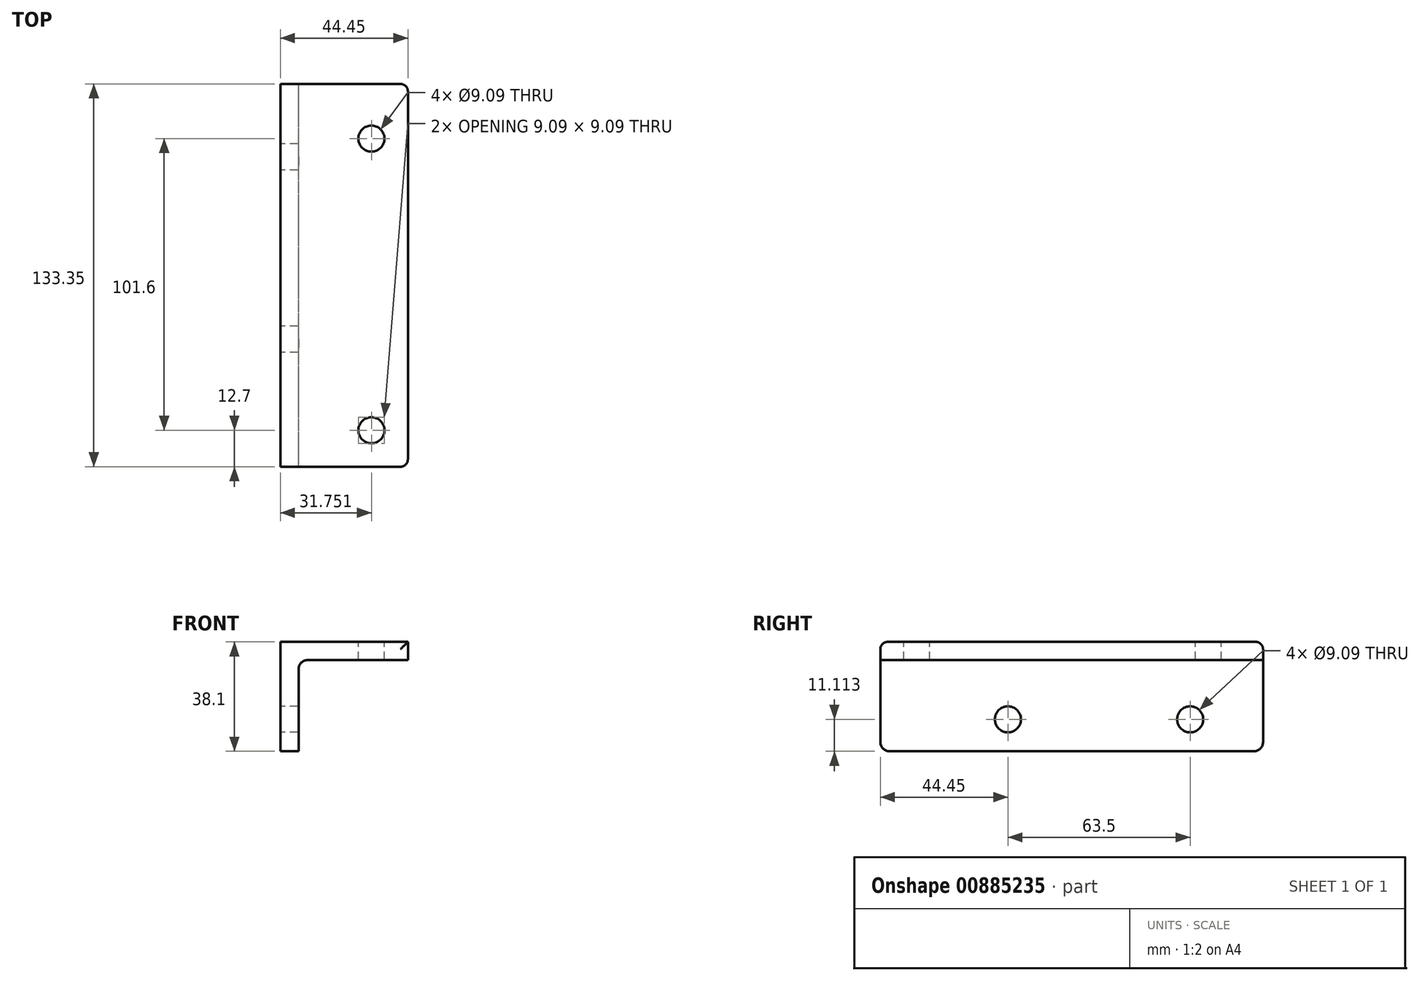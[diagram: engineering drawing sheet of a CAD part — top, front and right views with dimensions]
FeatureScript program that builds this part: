
annotation { "Feature Type Name" : "Feature", "Feature Type Description" : "" }
export const myFeature = defineFeature(function(context is Context, id is Id, definition is map)
    precondition{}
    {
        {
            var Q0;
            Q0=qCreatedBy(makeId("Front.planeOp"),FACE);
            var sketch = newSketch(context, id + "F0", { "sketchPlane" : qUnion([Q0])});
            skLineSegment(sketch, "E0", {"start": v(-29.69, -25.19) * mm, "end": v(-29.69, 12.91) * mm});
            skLineSegment(sketch, "E1", {"start": v(-29.69, 12.91) * mm, "end": v(14.76, 12.91) * mm});
            skLineSegment(sketch, "E2", {"start": v(14.76, 12.91) * mm, "end": v(14.76, 6.56) * mm});
            skLineSegment(sketch, "E3", {"start": v(14.76, 6.56) * mm, "end": v(-23.34, 6.56) * mm});
            skLineSegment(sketch, "E4", {"start": v(-23.34, 6.56) * mm, "end": v(-23.34, -25.19) * mm});
            skLineSegment(sketch, "E5", {"start": v(-23.34, -25.19) * mm, "end": v(-29.69, -25.19) * mm});
            skSolve(sketch);
        }
        {
            var Q0;
            Q0=makeQuery(id+"F0.imprint","IMPRINT",FACE,{"disambiguationData":[TD([[makeQuery(id+"F0.imprint","IMPRINT",EDGE,{"derivedFrom":sQuery(id+"F0.wireOp",EDGE,"E0")}),-1.0]])]});
            extrude(context, id + "F1", {"entities" : qUnion([Q0]), "depth" : 133.35 * mm, "offsetDistance" : 25.4 * mm});
        }
        {
            var Q0;
            Q0=makeQuery(id+"F1.opExtrude","SWEPT_FACE",FACE,{"disambiguationData":[OSD([sQuery(id+"F0.wireOp",EDGE,"E0")])]});
            var sketch = newSketch(context, id + "F2", { "sketchPlane" : qUnion([Q0])});
            skLineSegment(sketch, "E6", {"start": v(0, 12.91) * mm, "end": v(0, -14.08) * mm, "construction": true});
            skLineSegment(sketch, "E7", {"start": v(0, -14.08) * mm, "end": v(25.4, -14.08) * mm, "construction": true});
            skLineSegment(sketch, "E8", {"start": v(25.4, -14.08) * mm, "end": v(88.9, -14.08) * mm, "construction": true});
            skCircle(sketch, "E9", {"center": v(25.4, -14.08) * mm, "radius": 4.55 * mm});
            skCircle(sketch, "E10", {"center": v(88.9, -14.08) * mm, "radius": 4.55 * mm});
            skSolve(sketch);
        }
        {
            var Q0;
            Q0=makeQuery(id+"F2.imprint","IMPRINT",FACE,{"disambiguationData":[TD([[makeQuery(id+"F2.imprint","IMPRINT",EDGE,{"derivedFrom":sQuery(id+"F2.wireOp",EDGE,"E9")}),1.0]])]});
            var Q1;
            Q1=makeQuery(id+"F2.imprint","IMPRINT",FACE,{"disambiguationData":[TD([[makeQuery(id+"F2.imprint","IMPRINT",EDGE,{"derivedFrom":sQuery(id+"F2.wireOp",EDGE,"E10")}),1.0]])]});
            extrude(context, id + "F3", {"entities" : qUnion([Q0, Q1]), "operationType" : NewBodyOperationType.REMOVE, "oppositeDirection" : true, "depth" : 25.4 * mm, "offsetDistance" : 25.4 * mm});
        }
        {
            var Q0;
            Q0=makeQuery(id+"F1.opExtrude","SWEPT_FACE",FACE,{"disambiguationData":[OSD([sQuery(id+"F0.wireOp",EDGE,"E1")])]});
            var sketch = newSketch(context, id + "F4", { "sketchPlane" : qUnion([Q0])});
            skLineSegment(sketch, "E11", {"start": v(14.76, 0) * mm, "end": v(2.06, 0) * mm, "construction": true});
            skLineSegment(sketch, "E12", {"start": v(2.06, 0) * mm, "end": v(2.06, -19.05) * mm, "construction": true});
            skLineSegment(sketch, "E13", {"start": v(2.06, -19.05) * mm, "end": v(2.06, -120.65) * mm, "construction": true});
            skCircle(sketch, "E14", {"center": v(2.06, -120.65) * mm, "radius": 4.55 * mm});
            skCircle(sketch, "E15", {"center": v(2.06, -19.05) * mm, "radius": 4.55 * mm});
            skSolve(sketch);
        }
        {
            var Q0;
            Q0=makeQuery(id+"F4.imprint","IMPRINT",FACE,{"disambiguationData":[TD([[makeQuery(id+"F4.imprint","IMPRINT",EDGE,{"derivedFrom":sQuery(id+"F4.wireOp",EDGE,"E14")}),1.0]])]});
            var Q1;
            Q1=makeQuery(id+"F4.imprint","IMPRINT",FACE,{"disambiguationData":[TD([[makeQuery(id+"F4.imprint","IMPRINT",EDGE,{"derivedFrom":sQuery(id+"F4.wireOp",EDGE,"E15")}),1.0]])]});
            extrude(context, id + "F5", {"entities" : qUnion([Q0, Q1]), "operationType" : NewBodyOperationType.REMOVE, "oppositeDirection" : true, "depth" : 25.4 * mm, "offsetDistance" : 25.4 * mm});
        }
        {
            var Q0;
            Q0=makeQuery(id+"F1.opExtrude","CAP_EDGE",EDGE,{"disambiguationData":[OSD([sQuery(id+"F0.wireOp",EDGE,"E2")])],"isStart":false});
            var Q1;
            Q1=makeQuery(id+"F1.opExtrude","CAP_EDGE",EDGE,{"disambiguationData":[OSD([sQuery(id+"F0.wireOp",EDGE,"E1")])],"isStart":false});
            var Q2;
            Q2=makeQuery(id+"F1.opExtrude","CAP_EDGE",EDGE,{"disambiguationData":[OSD([sQuery(id+"F0.wireOp",EDGE,"E1")])],"isStart":true});
            var Q3;
            Q3=makeQuery(id+"F1.opExtrude","CAP_EDGE",EDGE,{"disambiguationData":[OSD([sQuery(id+"F0.wireOp",EDGE,"E2")])],"isStart":true});
            fillet(context, id + "F6", {"entities" : qUnion([Q0, Q1, Q2, Q3]), "radius" : 2.54 * mm, "allowEdgeOverflow" : false});
        }
        {
            var Q0;
            Q0=makeQuery(id+"F1.opExtrude","CAP_EDGE",EDGE,{"disambiguationData":[OSD([sQuery(id+"F0.wireOp",EDGE,"E5")])],"isStart":false});
            var Q1;
            Q1=makeQuery(id+"F1.opExtrude","CAP_EDGE",EDGE,{"disambiguationData":[OSD([sQuery(id+"F0.wireOp",EDGE,"E5")])],"isStart":true});
            var Q2;
            Q2=makeQuery(id+"F1.opExtrude","CAP_EDGE",EDGE,{"disambiguationData":[OSD([sQuery(id+"F0.wireOp",EDGE,"E2")])],"isStart":true});
            var Q3;
            Q3=makeQuery(id+"F1.opExtrude","SWEPT_EDGE",EDGE,{"disambiguationData":[OSD([sQuery(id+"F0.wireOp",EDGE,"E3"),sQuery(id+"F0.wireOp",EDGE,"E4")])]});
            fillet(context, id + "F7", {"entities" : qUnion([Q0, Q1, Q2, Q3]), "radius" : 3.17 * mm, "allowEdgeOverflow" : false});
        }
    });
